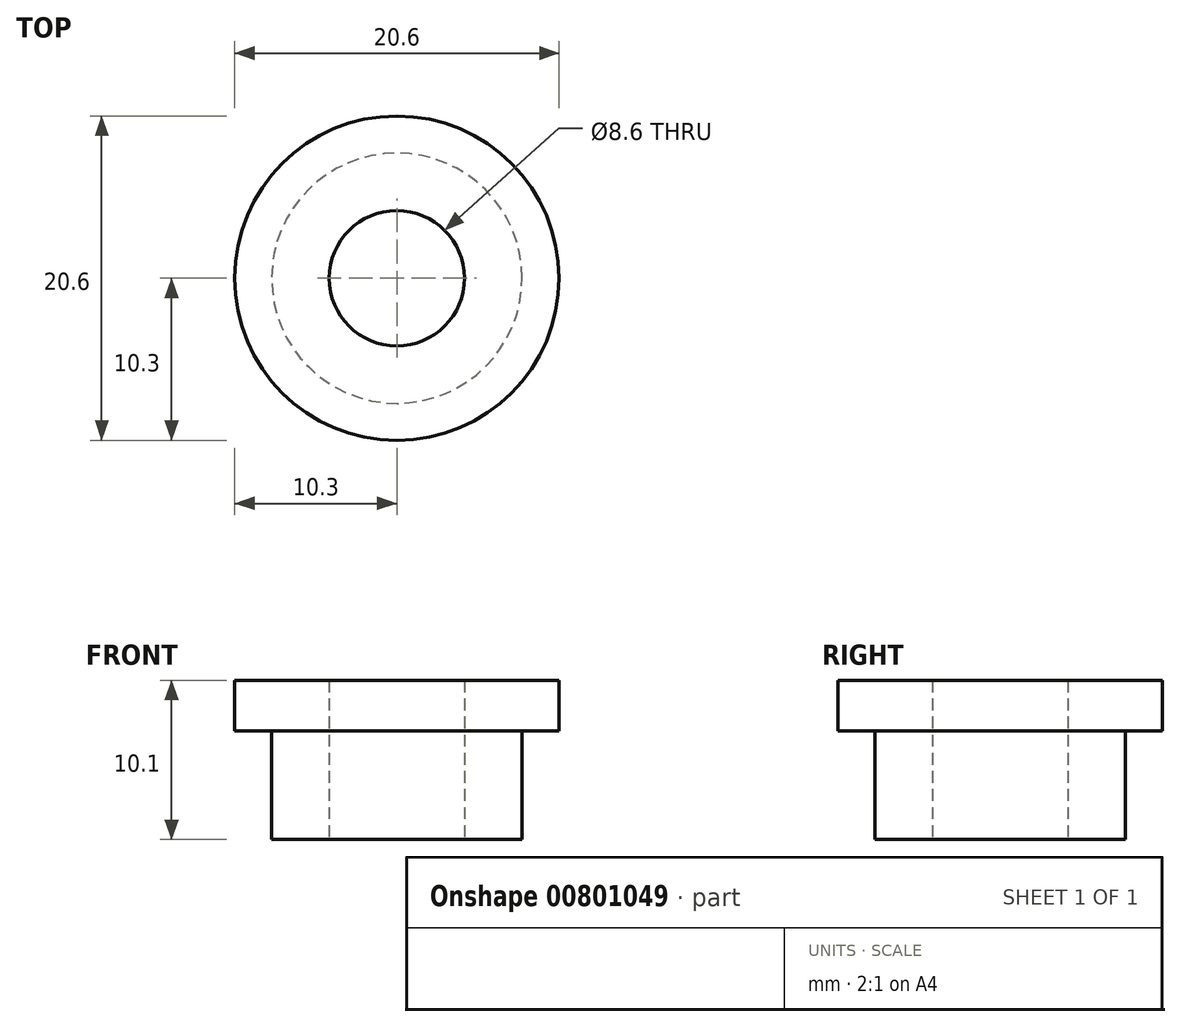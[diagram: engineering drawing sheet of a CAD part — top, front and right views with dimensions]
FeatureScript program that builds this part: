
annotation { "Feature Type Name" : "Feature", "Feature Type Description" : "" }
export const myFeature = defineFeature(function(context is Context, id is Id, definition is map)
    precondition{}
    {
        {
            var Q0;
            Q0=qCreatedBy(makeId("Front.planeOp"),FACE);
            var sketch = newSketch(context, id + "F0", { "sketchPlane" : qUnion([Q0])});
            skLineSegment(sketch, "E0", {"start": v(0, 0) * mm, "end": v(0, -10.1) * mm});
            skLineSegment(sketch, "E1", {"start": v(0, -10.1) * mm, "end": v(7.95, -10.1) * mm});
            skLineSegment(sketch, "E2", {"start": v(7.95, -10.1) * mm, "end": v(7.95, -3.2) * mm});
            skLineSegment(sketch, "E3", {"start": v(7.95, -3.2) * mm, "end": v(10.3, -3.2) * mm});
            skLineSegment(sketch, "E4", {"start": v(10.3, -3.2) * mm, "end": v(10.3, 0) * mm});
            skLineSegment(sketch, "E5", {"start": v(10.3, 0) * mm, "end": v(0, 0) * mm});
            skSolve(sketch);
        }
        {
            var Q0;
            Q0=makeQuery(id+"F0.imprint","IMPRINT",FACE,{"disambiguationData":[TD([[makeQuery(id+"F0.imprint","IMPRINT",EDGE,{"derivedFrom":sQuery(id+"F0.wireOp",EDGE,"E0")}),1.0]])]});
            var Q1;
            Q1=sQuery(id+"F0.wireOp",EDGE,"E0");
            revolve(context, id + "F1", {"surfaceOperationType" : NewSurfaceOperationType.NEW, "entities" : qUnion([Q0]), "axis" : qUnion([Q1]), "revolveType" : RevolveType.FULL});
        }
        {
            var Q0;
            Q0=makeQuery(id+"F1.opRevolve","SWEPT_FACE",FACE,{"disambiguationData":[OSD([sQuery(id+"F0.wireOp",EDGE,"E1")])]});
            cPlane(context, id + "F2", {"entities" : qUnion([Q0]), "cplaneType" : CPlaneType.OFFSET, "offset" : 0 * mm, "width" : 150 * mm, "height" : 150 * mm});
        }
        {
            var Q0;
            Q0=qCreatedBy(id+"F2.planeOp",FACE);
            var sketch = newSketch(context, id + "F3", { "sketchPlane" : qUnion([Q0])});
            skCircle(sketch, "E6", {"center": v(0, 0) * mm, "radius": 4.3 * mm});
            skSolve(sketch);
        }
        {
            var Q0;
            Q0 = qSketchRegion(id + "F3", true);
            extrude(context, id + "F4", {"entities" : qUnion([Q0]), "operationType" : NewBodyOperationType.REMOVE, "endBound" : BoundingType.THROUGH_ALL, "oppositeDirection" : true, "depth" : 25 * mm, "offsetDistance" : 25 * mm});
        }
    });
